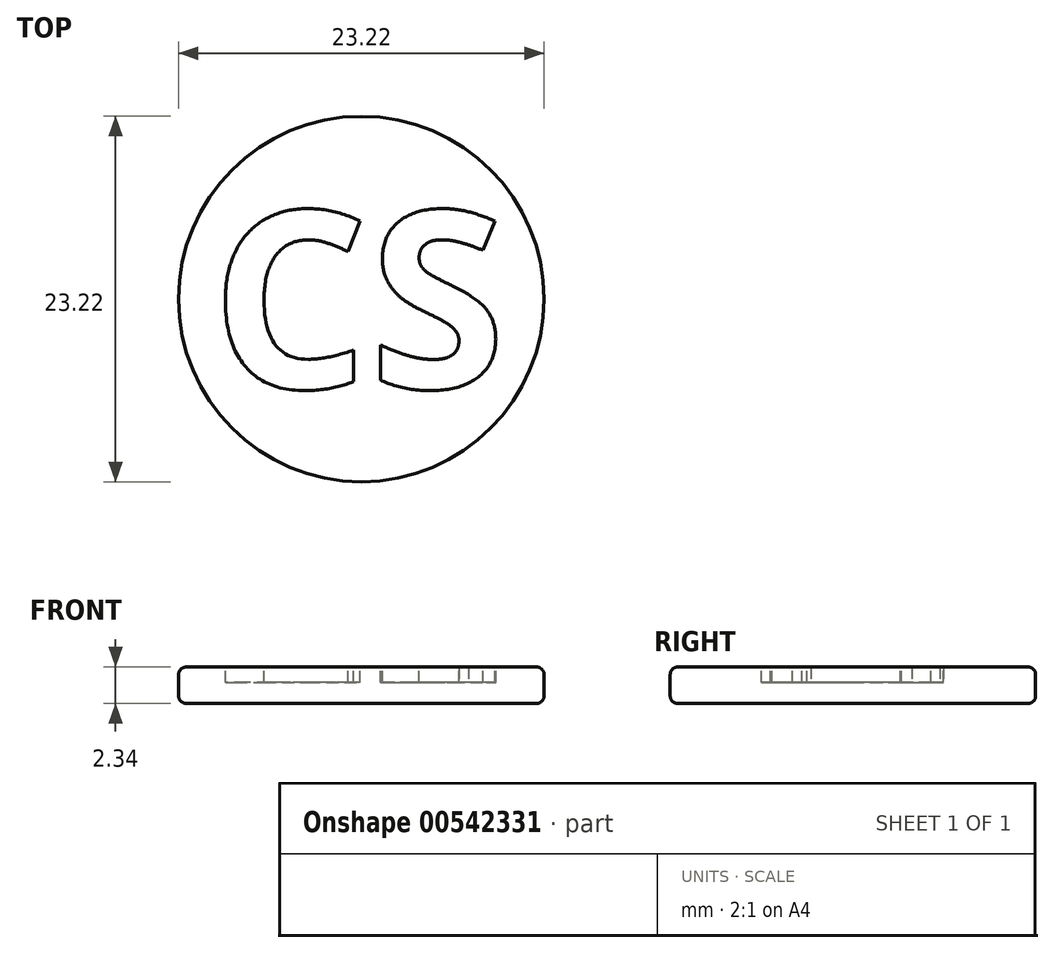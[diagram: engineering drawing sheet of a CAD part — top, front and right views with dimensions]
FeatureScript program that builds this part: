
annotation { "Feature Type Name" : "Feature", "Feature Type Description" : "" }
export const myFeature = defineFeature(function(context is Context, id is Id, definition is map)
    precondition{}
    {
        {
            var Q0;
            Q0=qCreatedBy(makeId("Top.planeOp"),FACE);
            var sketch = newSketch(context, id + "F0", { "sketchPlane" : qUnion([Q0])});
            skCircle(sketch, "E0", {"center": v(0, 0) * mm, "radius": 11.6 * mm});
            skSolve(sketch);
        }
        {
            var Q0;
            Q0 = qSketchRegion(id + "F0", true);
            extrude(context, id + "F1", {"entities" : qUnion([Q0]), "endBound" : BoundingType.SYMMETRIC, "depth" : 2.33 * mm, "offsetDistance" : 25 * mm});
        }
        {
            var Q0;
            Q0=makeQuery(id+"F1.opExtrude","CAP_EDGE",EDGE,{"disambiguationData":[OSD([sQuery(id+"F0.wireOp",EDGE,"E0")])],"isStart":true});
            var Q1;
            Q1=makeQuery(id+"F1.opExtrude","CAP_EDGE",EDGE,{"disambiguationData":[OSD([sQuery(id+"F0.wireOp",EDGE,"E0")])],"isStart":false});
            fillet(context, id + "F2", {"entities" : qUnion([Q0, Q1]), "radius" : 0.5 * mm, "tangentPropagation" : true, "allowEdgeOverflow" : false});
        }
        {
            var Q0;
            Q0=makeQuery(id+"F1.opExtrude","CAP_FACE",FACE,{"disambiguationData":[OSD([sQuery(id+"F0.wireOp",EDGE,"E0")])],"isStart":false});
            var sketch = newSketch(context, id + "F3", { "sketchPlane" : qUnion([Q0])});
            skText(sketch, "E1", { "text": "CS", "fontName": "OpenSans-Bold.ttf"});
            const initialGuessF3  = {"E1": [-0.00955, -0.00566, 1, 0, 0.01134]};
            skSetInitialGuess(sketch, initialGuessF3);
            skSolve(sketch);
        }
        {
            var Q0;
            Q0 = qSketchRegion(id + "F3", true);
            extrude(context, id + "F4", {"entities" : qUnion([Q0]), "operationType" : NewBodyOperationType.REMOVE, "oppositeDirection" : true, "depth" : 1 * mm, "offsetDistance" : 25 * mm});
        }
    });
